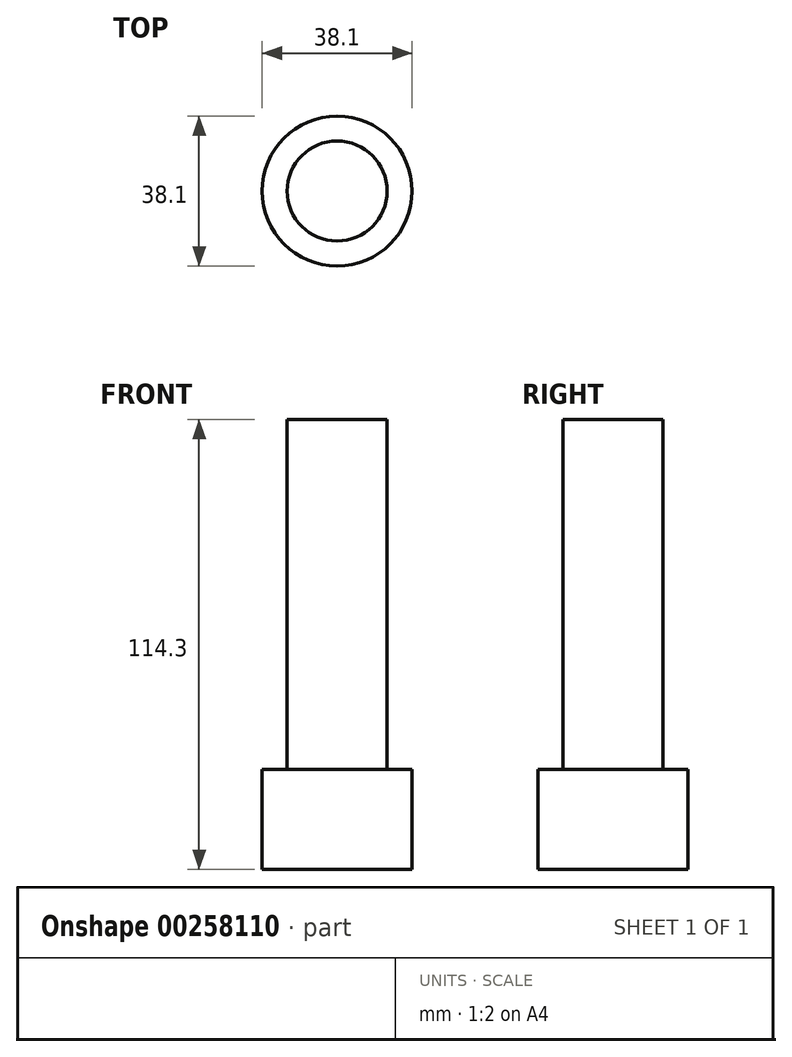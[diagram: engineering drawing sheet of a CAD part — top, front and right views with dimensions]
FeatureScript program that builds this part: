
annotation { "Feature Type Name" : "Feature", "Feature Type Description" : "" }
export const myFeature = defineFeature(function(context is Context, id is Id, definition is map)
    precondition{}
    {
        {
            var Q0;
            Q0=qCreatedBy(makeId("Top.planeOp"),FACE);
            var sketch = newSketch(context, id + "F0", { "sketchPlane" : qUnion([Q0])});
            skCircle(sketch, "E0", {"center": v(0, 0) * mm, "radius": 12.7 * mm});
            skSolve(sketch);
        }
        {
            var Q0;
            Q0=qSketchRegion(id+"F0",true);
            extrude(context, id + "F1", {"entities" : qUnion([Q0]), "depth" : 88.9 * mm});
        }
        {
            var Q0;
            Q0=qCreatedBy(makeId("Top.planeOp"),FACE);
            var sketch = newSketch(context, id + "F2", { "sketchPlane" : qUnion([Q0])});
            skCircle(sketch, "E1", {"center": v(0, 0) * mm, "radius": 19.05 * mm});
            skSolve(sketch);
        }
        {
            var Q0;
            Q0=qSketchRegion(id+"F2",true);
            extrude(context, id + "F3", {"entities" : qUnion([Q0]), "operationType" : NewBodyOperationType.ADD, "oppositeDirection" : true, "depth" : 25.4 * mm});
        }
    });
